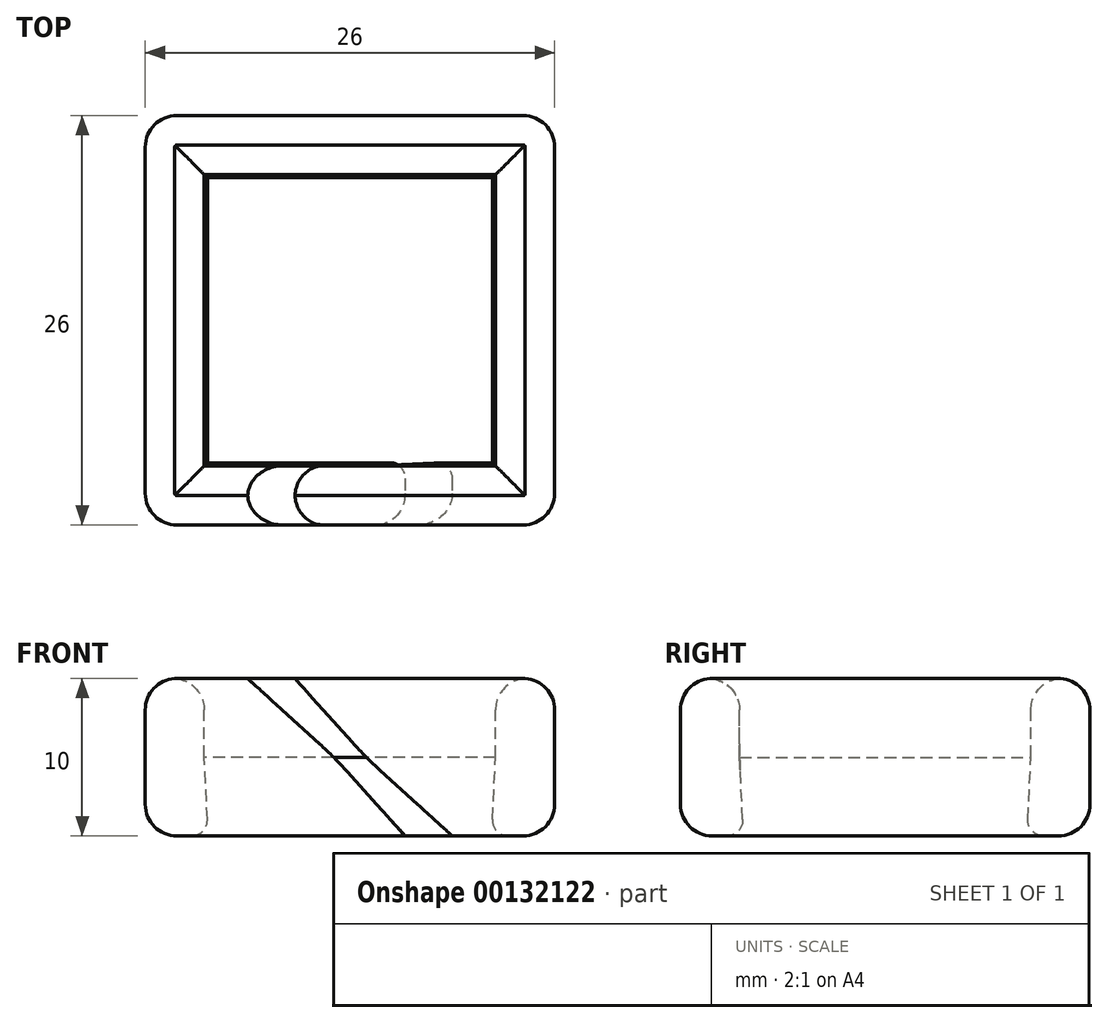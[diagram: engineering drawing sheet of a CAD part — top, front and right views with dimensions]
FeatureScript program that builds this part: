
annotation { "Feature Type Name" : "Feature", "Feature Type Description" : "" }
export const myFeature = defineFeature(function(context is Context, id is Id, definition is map)
    precondition{}
    {
        {
            var Q0;
            Q0=qCreatedBy(makeId("Top.planeOp"),FACE);
            var sketch = newSketch(context, id + "F0", { "sketchPlane" : qUnion([Q0])});
            skLineSegment(sketch, "E0.bottom", {"start": v(9, -9) * mm, "end": v(-9, -9) * mm});
            skLineSegment(sketch, "E0.top", {"start": v(9, 9) * mm, "end": v(-9, 9) * mm});
            skLineSegment(sketch, "E0.left", {"start": v(9, -9) * mm, "end": v(9, 9) * mm});
            skLineSegment(sketch, "E0.right", {"start": v(-9, -9) * mm, "end": v(-9, 9) * mm});
            skPoint(sketch, "E0.middle", {"position": v(0, 0) * mm});
            skLineSegment(sketch, "E1.bottom", {"start": v(13, -13) * mm, "end": v(-13, -13) * mm});
            skLineSegment(sketch, "E1.top", {"start": v(13, 13) * mm, "end": v(-13, 13) * mm});
            skLineSegment(sketch, "E1.left", {"start": v(13, -13) * mm, "end": v(13, 13) * mm});
            skLineSegment(sketch, "E1.right", {"start": v(-13, -13) * mm, "end": v(-13, 13) * mm});
            skLineSegment(sketch, "E2", {"start": v(-9, -9) * mm, "end": v(-13, -13) * mm});
            skLineSegment(sketch, "E3", {"start": v(9, 9) * mm, "end": v(13, 13) * mm});
            skLineSegment(sketch, "E4", {"start": v(0, -9) * mm, "end": v(0, -13) * mm, "construction": true});
            skLineSegment(sketch, "E5.0", {"start": v(5, -9) * mm, "end": v(5, -13) * mm, "construction": true});
            skLineSegment(sketch, "E6.0", {"start": v(6.5, -9) * mm, "end": v(6.5, -13) * mm});
            skLineSegment(sketch, "E7.0", {"start": v(3.5, -9) * mm, "end": v(3.5, -13) * mm});
            skSolve(sketch);
        }
        {
            var Q0;
            Q0=qCreatedBy(makeId("Top.planeOp"),FACE);
            cPlane(context, id + "F1", {"entities" : qUnion([Q0]), "cplaneType" : CPlaneType.OFFSET, "offset" : 5 * mm, "width" : 150 * mm, "height" : 150 * mm});
        }
        {
            var Q0;
            Q0=qCreatedBy(id+"F1.planeOp",FACE);
            var sketch = newSketch(context, id + "F2", { "sketchPlane" : qUnion([Q0])});
            skPoint(sketch, "E8.0", {"position": v(0, 0) * mm});
            skLineSegment(sketch, "E9.0", {"start": v(13, 13) * mm, "end": v(-13, 13) * mm});
            skLineSegment(sketch, "E10.0", {"start": v(-13, -13) * mm, "end": v(-13, 13) * mm});
            skLineSegment(sketch, "E11.0", {"start": v(13, -13) * mm, "end": v(-13, -13) * mm});
            skLineSegment(sketch, "E12.0", {"start": v(13, -13) * mm, "end": v(13, 13) * mm});
            skLineSegment(sketch, "E13.bottom", {"start": v(9.25, -9.25) * mm, "end": v(-9.25, -9.25) * mm});
            skLineSegment(sketch, "E13.top", {"start": v(9.25, 9.25) * mm, "end": v(-9.25, 9.25) * mm});
            skLineSegment(sketch, "E13.left", {"start": v(9.25, -9.25) * mm, "end": v(9.25, 9.25) * mm});
            skLineSegment(sketch, "E13.right", {"start": v(-9.25, -9.25) * mm, "end": v(-9.25, 9.25) * mm});
            skLineSegment(sketch, "E14", {"start": v(-13, -13) * mm, "end": v(-9.25, -9.25) * mm});
            skLineSegment(sketch, "E15", {"start": v(9.25, 9.25) * mm, "end": v(13, 13) * mm});
            skLineSegment(sketch, "E16", {"start": v(0, -9.25) * mm, "end": v(0, -13) * mm, "construction": true});
            skLineSegment(sketch, "E17.0", {"start": v(-1, -9.25) * mm, "end": v(-1, -13) * mm});
            skLineSegment(sketch, "E18.MirrorCS", {"start": v(1, -9.25) * mm, "end": v(1, -13) * mm});
            skSolve(sketch);
        }
        {
            var Q0;
            Q0=qCreatedBy(makeId("Top.planeOp"),FACE);
            cPlane(context, id + "F3", {"entities" : qUnion([Q0]), "cplaneType" : CPlaneType.OFFSET, "offset" : 10 * mm, "width" : 150 * mm, "height" : 150 * mm});
        }
        {
            var Q0;
            Q0=qCreatedBy(id+"F3.planeOp",FACE);
            var sketch = newSketch(context, id + "F4", { "sketchPlane" : qUnion([Q0])});
            skPoint(sketch, "E19.0", {"position": v(0, 0) * mm});
            skLineSegment(sketch, "E20.0", {"start": v(13, 13) * mm, "end": v(-13, 13) * mm});
            skLineSegment(sketch, "E21.0", {"start": v(13, -13) * mm, "end": v(13, 13) * mm});
            skLineSegment(sketch, "E21.1", {"start": v(13, -13) * mm, "end": v(-13, -13) * mm});
            skLineSegment(sketch, "E21.2", {"start": v(-13, -13) * mm, "end": v(-13, 13) * mm});
            skLineSegment(sketch, "E22.bottom", {"start": v(9.25, -9.25) * mm, "end": v(-9.25, -9.25) * mm});
            skLineSegment(sketch, "E22.top", {"start": v(9.25, 9.25) * mm, "end": v(-9.25, 9.25) * mm});
            skLineSegment(sketch, "E22.left", {"start": v(9.25, -9.25) * mm, "end": v(9.25, 9.25) * mm});
            skLineSegment(sketch, "E22.right", {"start": v(-9.25, -9.25) * mm, "end": v(-9.25, 9.25) * mm});
            skLineSegment(sketch, "E23", {"start": v(-13, -13) * mm, "end": v(-9.25, -9.25) * mm});
            skLineSegment(sketch, "E24", {"start": v(9.25, 9.25) * mm, "end": v(13, 13) * mm});
            skLineSegment(sketch, "E25", {"start": v(0, -9.25) * mm, "end": v(0, -13) * mm, "construction": true});
            skLineSegment(sketch, "E26.0", {"start": v(-5, -9.25) * mm, "end": v(-5, -13) * mm, "construction": true});
            skLineSegment(sketch, "E27.0", {"start": v(-6.5, -9.25) * mm, "end": v(-6.5, -13) * mm});
            skLineSegment(sketch, "E28.0", {"start": v(-3.5, -9.25) * mm, "end": v(-3.5, -13) * mm});
            skSolve(sketch);
        }
        {
            var Q0;
            Q0=makeQuery(id+"F0.imprint","IMPRINT",FACE,{"disambiguationData":[TD([[makeQuery(id+"F0.imprint","IMPRINT",EDGE,{"derivedFrom":sQuery(id+"F0.wireOp",EDGE,"E0.top")}),-1.0]])]});
            var Q1;
            Q1=makeQuery(id+"F2.imprint","IMPRINT",FACE,{"disambiguationData":[TD([[makeQuery(id+"F2.imprint","IMPRINT",EDGE,{"derivedFrom":sQuery(id+"F2.wireOp",EDGE,"E9.0")}),1.0]])]});
            loft(context, id + "F5", {"sheetProfilesArray" : [{ "sheetProfileEntities" : qUnion([Q0]) }, { "sheetProfileEntities" : qUnion([Q1]) }]});
        }
        {
            var Q1;
            Q1=makeQuery(id+"F2.imprint","IMPRINT",FACE,{"disambiguationData":[TD([[makeQuery(id+"F2.imprint","IMPRINT",EDGE,{"derivedFrom":sQuery(id+"F2.wireOp",EDGE,"E9.0")}),1.0]])]});
            var Q2;
            Q2=makeQuery(id+"F4.imprint","IMPRINT",FACE,{"disambiguationData":[TD([[makeQuery(id+"F4.imprint","IMPRINT",EDGE,{"derivedFrom":sQuery(id+"F4.wireOp",EDGE,"E20.0")}),1.0]])]});
            loft(context, id + "F6", {"operationType" : NewBodyOperationType.ADD, "sheetProfilesArray" : [{ "sheetProfileEntities" : qUnion([Q1]) }, { "sheetProfileEntities" : qUnion([Q2]) }]});
        }
        {
            var Q1;
            {var subQ0=sQuery(id+"F0.wireOp",EDGE,"E2");Q1=makeQuery(id+"F0.imprint","IMPRINT",FACE,{"disambiguationData":[TD([[makeQuery(id+"F0.imprint","IMPRINT",EDGE,{"derivedFrom":subQ0}),1.0]])]});}
            var Q2;
            {var subQ0=sQuery(id+"F2.wireOp",EDGE,"E14");Q2=makeQuery(id+"F2.imprint","IMPRINT",FACE,{"disambiguationData":[TD([[makeQuery(id+"F2.imprint","IMPRINT",EDGE,{"derivedFrom":subQ0}),-1.0]])]});}
            loft(context, id + "F7", {"operationType" : NewBodyOperationType.ADD, "sheetProfilesArray" : [{ "sheetProfileEntities" : qUnion([Q1]) }, { "sheetProfileEntities" : qUnion([Q2]) }]});
        }
        {
            var Q1;
            {var subQ0=sQuery(id+"F2.wireOp",EDGE,"E14");Q1=makeQuery(id+"F2.imprint","IMPRINT",FACE,{"disambiguationData":[TD([[makeQuery(id+"F2.imprint","IMPRINT",EDGE,{"derivedFrom":subQ0}),-1.0]])]});}
            var Q2;
            {var subQ0=sQuery(id+"F4.wireOp",EDGE,"E23");Q2=makeQuery(id+"F4.imprint","IMPRINT",FACE,{"disambiguationData":[TD([[makeQuery(id+"F4.imprint","IMPRINT",EDGE,{"derivedFrom":subQ0}),-1.0]])]});}
            loft(context, id + "F8", {"operationType" : NewBodyOperationType.ADD, "sheetProfilesArray" : [{ "sheetProfileEntities" : qUnion([Q1]) }, { "sheetProfileEntities" : qUnion([Q2]) }]});
        }
        {
            var Q1;
            {var subQ3=sQuery(id+"F0.wireOp",EDGE,"E0.left");Q1=makeQuery(id+"F0.imprint","IMPRINT",FACE,{"disambiguationData":[TD([[makeQuery(id+"F0.imprint","IMPRINT",EDGE,{"derivedFrom":subQ3}),-1.0]])]});}
            var Q2;
            {var subQ3=sQuery(id+"F2.wireOp",EDGE,"E12.0");Q2=makeQuery(id+"F2.imprint","IMPRINT",FACE,{"disambiguationData":[TD([[makeQuery(id+"F2.imprint","IMPRINT",EDGE,{"derivedFrom":subQ3}),1.0]])]});}
            loft(context, id + "F9", {"operationType" : NewBodyOperationType.ADD, "sheetProfilesArray" : [{ "sheetProfileEntities" : qUnion([Q1]) }, { "sheetProfileEntities" : qUnion([Q2]) }]});
        }
        {
            var Q1;
            {var subQ3=sQuery(id+"F2.wireOp",EDGE,"E12.0");Q1=makeQuery(id+"F2.imprint","IMPRINT",FACE,{"disambiguationData":[TD([[makeQuery(id+"F2.imprint","IMPRINT",EDGE,{"derivedFrom":subQ3}),1.0]])]});}
            var Q2;
            {var subQ4=sQuery(id+"F4.wireOp",EDGE,"E21.0");Q2=makeQuery(id+"F4.imprint","IMPRINT",FACE,{"disambiguationData":[TD([[makeQuery(id+"F4.imprint","IMPRINT",EDGE,{"derivedFrom":subQ4}),1.0]])]});}
            loft(context, id + "F10", {"operationType" : NewBodyOperationType.ADD, "sheetProfilesArray" : [{ "sheetProfileEntities" : qUnion([Q1]) }, { "sheetProfileEntities" : qUnion([Q2]) }]});
        }
        {
            var Q0;
            Q0=makeQuery(id+"F6.opLoft","MID_CAP_EDGE",EDGE,{"disambiguationData":[OSD([sQuery(id+"F4.wireOp",EDGE,"E22.top"),sQuery(id+"F4.wireOp",EDGE,"E22.left"),sQuery(id+"F4.wireOp",EDGE,"E22.right"),sQuery(id+"F4.wireOp",EDGE,"E24")])],"capPos":1.0});
            var Q1;
            Q1=makeQuery(id+"F10.opLoft","MID_CAP_EDGE",EDGE,{"disambiguationData":[OSD([sQuery(id+"F4.wireOp",EDGE,"E22.bottom"),sQuery(id+"F4.wireOp",EDGE,"E22.top"),sQuery(id+"F4.wireOp",EDGE,"E22.left"),sQuery(id+"F4.wireOp",EDGE,"E24")])],"capPos":1.0});
            var Q2;
            Q2=makeQuery(id+"F10.opLoft","MID_CAP_EDGE",EDGE,{"disambiguationData":[OSD([sQuery(id+"F4.wireOp",EDGE,"E22.bottom"),sQuery(id+"F4.wireOp",EDGE,"E22.left"),sQuery(id+"F4.wireOp",EDGE,"ebbac85e-4af3-46f9-9d82-f182fd674b780.MirrorCS")])],"capPos":1.0});
            var Q3;
            Q3=makeQuery(id+"F6.opLoft","MID_CAP_EDGE",EDGE,{"disambiguationData":[OSD([sQuery(id+"F4.wireOp",EDGE,"E22.bottom"),sQuery(id+"F4.wireOp",EDGE,"E22.top"),sQuery(id+"F4.wireOp",EDGE,"E22.right"),sQuery(id+"F4.wireOp",EDGE,"E23")])],"capPos":1.0});
            var Q4;
            Q4=makeQuery(id+"F8.opLoft","MID_CAP_EDGE",EDGE,{"disambiguationData":[OSD([sQuery(id+"F4.wireOp",EDGE,"E22.bottom"),sQuery(id+"F4.wireOp",EDGE,"E22.right"),sQuery(id+"F4.wireOp",EDGE,"E23"),sQuery(id+"F4.wireOp",EDGE,"E27.0")])],"capPos":1.0});
            var Q5;
            Q5=makeQuery(id+"F6.opLoft","MID_CAP_EDGE",EDGE,{"disambiguationData":[OSD([sQuery(id+"F4.wireOp",EDGE,"E20.0"),sQuery(id+"F4.wireOp",EDGE,"E21.1"),sQuery(id+"F4.wireOp",EDGE,"E21.2"),sQuery(id+"F4.wireOp",EDGE,"E23")])],"capPos":1.0});
            var Q6;
            Q6=makeQuery(id+"F8.opLoft","MID_CAP_EDGE",EDGE,{"disambiguationData":[OSD([sQuery(id+"F4.wireOp",EDGE,"E21.1"),sQuery(id+"F4.wireOp",EDGE,"E21.2"),sQuery(id+"F4.wireOp",EDGE,"E23"),sQuery(id+"F4.wireOp",EDGE,"E27.0")])],"capPos":1.0});
            var Q7;
            Q7=makeQuery(id+"F10.opLoft","MID_CAP_EDGE",EDGE,{"disambiguationData":[OSD([sQuery(id+"F4.wireOp",EDGE,"E21.0"),sQuery(id+"F4.wireOp",EDGE,"E21.1"),sQuery(id+"F4.wireOp",EDGE,"ebbac85e-4af3-46f9-9d82-f182fd674b780.MirrorCS")])],"capPos":1.0});
            var Q8;
            Q8=makeQuery(id+"F6.opLoft","MID_CAP_EDGE",EDGE,{"disambiguationData":[OSD([sQuery(id+"F4.wireOp",EDGE,"E20.0"),sQuery(id+"F4.wireOp",EDGE,"E21.0"),sQuery(id+"F4.wireOp",EDGE,"E21.2"),sQuery(id+"F4.wireOp",EDGE,"E24")])],"capPos":1.0});
            var Q9;
            Q9=makeQuery(id+"F10.opLoft","MID_CAP_EDGE",EDGE,{"disambiguationData":[OSD([sQuery(id+"F4.wireOp",EDGE,"E20.0"),sQuery(id+"F4.wireOp",EDGE,"E21.0"),sQuery(id+"F4.wireOp",EDGE,"E21.1"),sQuery(id+"F4.wireOp",EDGE,"E24")])],"capPos":1.0});
            var Q10;
            {var subQ0=sQuery(id+"F4.wireOp",EDGE,"E24");var subQ1=sQuery(id+"F4.wireOp",EDGE,"E21.0");var subQ2=sQuery(id+"F4.wireOp",EDGE,"E20.0");var subQ3=sQuery(id+"F2.wireOp",EDGE,"E15");var subQ4=sQuery(id+"F2.wireOp",EDGE,"E12.0");var subQ5=sQuery(id+"F2.wireOp",EDGE,"E9.0");var subQ6=sQuery(id+"F0.wireOp",EDGE,"E3");var subQ7=sQuery(id+"F0.wireOp",EDGE,"E1.left");var subQ8=sQuery(id+"F0.wireOp",EDGE,"E1.top");var subQ9=makeQuery(id+"F6.boolean.opBoolean","MERGE",EDGE,{"derivedFrom":[makeQuery(id+"F5.opLoft","SWEPT_EDGE",EDGE,{"disambiguationData":[OSD([subQ8,subQ7,subQ6,subQ5,subQ4,subQ3])]}),makeQuery(id+"F6.opLoft","SWEPT_EDGE",EDGE,{"disambiguationData":[OSD([subQ5,subQ4,subQ3,subQ2,subQ1,subQ0])]})]});Q10=makeQuery(id+"F10.boolean.opBoolean","MERGE",EDGE,{"derivedFrom":[makeQuery(id+"F9.boolean.opBoolean","MERGE",EDGE,{"derivedFrom":[subQ9,makeQuery(id+"F9.opLoft","SWEPT_EDGE",EDGE,{"disambiguationData":[OSD([subQ8,subQ7,subQ6,subQ5,subQ4,subQ3])]})]}),makeQuery(id+"F9.boolean.opBoolean","SPLIT",EDGE,{"derivedFrom":subQ9}),makeQuery(id+"F10.opLoft","SWEPT_EDGE",EDGE,{"disambiguationData":[OSD([subQ5,subQ4,subQ3,subQ2,subQ1,subQ0])]})]});}
            var Q11;
            {var subQ0=sQuery(id+"F2.wireOp",EDGE,"E12.0");var subQ1=sQuery(id+"F2.wireOp",EDGE,"E11.0");Q11=makeQuery(id+"F10.boolean.opBoolean","MERGE",EDGE,{"derivedFrom":[makeQuery(id+"F9.opLoft","SWEPT_EDGE",EDGE,{"disambiguationData":[OSD([sQuery(id+"F0.wireOp",EDGE,"E1.bottom"),sQuery(id+"F0.wireOp",EDGE,"E1.left"),subQ1,subQ0])]}),makeQuery(id+"F10.opLoft","SWEPT_EDGE",EDGE,{"disambiguationData":[OSD([subQ1,subQ0,sQuery(id+"F4.wireOp",EDGE,"E21.0"),sQuery(id+"F4.wireOp",EDGE,"E21.1")])]})]});}
            var Q12;
            {var subQ0=sQuery(id+"F4.wireOp",EDGE,"E23");var subQ1=sQuery(id+"F4.wireOp",EDGE,"E21.2");var subQ2=sQuery(id+"F4.wireOp",EDGE,"E21.1");var subQ3=sQuery(id+"F2.wireOp",EDGE,"E14");var subQ4=sQuery(id+"F2.wireOp",EDGE,"E11.0");var subQ5=sQuery(id+"F2.wireOp",EDGE,"E10.0");var subQ6=sQuery(id+"F0.wireOp",EDGE,"E2");var subQ7=sQuery(id+"F0.wireOp",EDGE,"E1.right");var subQ8=sQuery(id+"F0.wireOp",EDGE,"E1.bottom");var subQ9=makeQuery(id+"F6.boolean.opBoolean","MERGE",EDGE,{"derivedFrom":[makeQuery(id+"F5.opLoft","SWEPT_EDGE",EDGE,{"disambiguationData":[OSD([subQ8,subQ7,subQ6,subQ5,subQ4,subQ3])]}),makeQuery(id+"F6.opLoft","SWEPT_EDGE",EDGE,{"disambiguationData":[OSD([subQ5,subQ4,subQ3,subQ2,subQ1,subQ0])]})]});Q12=makeQuery(id+"F8.boolean.opBoolean","MERGE",EDGE,{"derivedFrom":[makeQuery(id+"F7.boolean.opBoolean","MERGE",EDGE,{"derivedFrom":[subQ9,makeQuery(id+"F7.opLoft","SWEPT_EDGE",EDGE,{"disambiguationData":[OSD([subQ8,subQ7,subQ6,subQ5,subQ4,subQ3])]})]}),makeQuery(id+"F7.boolean.opBoolean","SPLIT",EDGE,{"derivedFrom":subQ9}),makeQuery(id+"F8.opLoft","SWEPT_EDGE",EDGE,{"disambiguationData":[OSD([subQ5,subQ4,subQ3,subQ2,subQ1,subQ0])]})]});}
            var Q13;
            Q13=makeQuery(id+"F9.opLoft","MID_CAP_EDGE",EDGE,{"disambiguationData":[OSD([sQuery(id+"F0.wireOp",EDGE,"E1.bottom"),sQuery(id+"F0.wireOp",EDGE,"E1.top"),sQuery(id+"F0.wireOp",EDGE,"E1.left"),sQuery(id+"F0.wireOp",EDGE,"E3")])],"capPos":0.0});
            var Q14;
            Q14=makeQuery(id+"F5.opLoft","MID_CAP_EDGE",EDGE,{"disambiguationData":[OSD([sQuery(id+"F0.wireOp",EDGE,"E1.top"),sQuery(id+"F0.wireOp",EDGE,"E1.left"),sQuery(id+"F0.wireOp",EDGE,"E1.right"),sQuery(id+"F0.wireOp",EDGE,"E3")])],"capPos":0.0});
            var Q15;
            Q15=makeQuery(id+"F9.opLoft","MID_CAP_EDGE",EDGE,{"disambiguationData":[OSD([sQuery(id+"F0.wireOp",EDGE,"E1.bottom"),sQuery(id+"F0.wireOp",EDGE,"E1.left"),sQuery(id+"F0.wireOp",EDGE,"E6.0")])],"capPos":0.0});
            var Q16;
            Q16=makeQuery(id+"F7.opLoft","MID_CAP_EDGE",EDGE,{"disambiguationData":[OSD([sQuery(id+"F0.wireOp",EDGE,"E1.bottom"),sQuery(id+"F0.wireOp",EDGE,"E1.right"),sQuery(id+"F0.wireOp",EDGE,"E2"),sQuery(id+"F0.wireOp",EDGE,"4b8213a9-0e5b-4562-8142-2c595d69f7cd0.MirrorCS")])],"capPos":0.0});
            var Q17;
            {var subQ0=sQuery(id+"F2.wireOp",EDGE,"E10.0");var subQ1=sQuery(id+"F2.wireOp",EDGE,"E9.0");Q17=makeQuery(id+"F6.boolean.opBoolean","MERGE",EDGE,{"derivedFrom":[makeQuery(id+"F5.opLoft","SWEPT_EDGE",EDGE,{"disambiguationData":[OSD([sQuery(id+"F0.wireOp",EDGE,"E1.top"),sQuery(id+"F0.wireOp",EDGE,"E1.right"),subQ1,subQ0])]}),makeQuery(id+"F6.opLoft","SWEPT_EDGE",EDGE,{"disambiguationData":[OSD([subQ1,subQ0,sQuery(id+"F4.wireOp",EDGE,"E20.0"),sQuery(id+"F4.wireOp",EDGE,"E21.2")])]})]});}
            var Q18;
            Q18=makeQuery(id+"F5.opLoft","MID_CAP_EDGE",EDGE,{"disambiguationData":[OSD([sQuery(id+"F0.wireOp",EDGE,"E1.bottom"),sQuery(id+"F0.wireOp",EDGE,"E1.top"),sQuery(id+"F0.wireOp",EDGE,"E1.right"),sQuery(id+"F0.wireOp",EDGE,"E2")])],"capPos":0.0});
            fillet(context, id + "F11", {"entities" : qUnion([Q0, Q1, Q2, Q3, Q4, Q5, Q6, Q7, Q8, Q9, Q10, Q11, Q12, Q13, Q14, Q15, Q16, Q17, Q18]), "radius" : 2 * mm, "tangentPropagation" : true, "allowEdgeOverflow" : false});
        }
        {
            var Q0;
            Q0=makeQuery(id+"F5.opLoft","MID_CAP_EDGE",EDGE,{"disambiguationData":[OSD([sQuery(id+"F0.wireOp",EDGE,"E0.top"),sQuery(id+"F0.wireOp",EDGE,"E0.left"),sQuery(id+"F0.wireOp",EDGE,"E0.right"),sQuery(id+"F0.wireOp",EDGE,"E3")])],"capPos":0.0});
            var Q1;
            Q1=makeQuery(id+"F5.opLoft","MID_CAP_EDGE",EDGE,{"disambiguationData":[OSD([sQuery(id+"F0.wireOp",EDGE,"E0.bottom"),sQuery(id+"F0.wireOp",EDGE,"E0.top"),sQuery(id+"F0.wireOp",EDGE,"E0.right"),sQuery(id+"F0.wireOp",EDGE,"E2")])],"capPos":0.0});
            var Q2;
            Q2=makeQuery(id+"F7.opLoft","MID_CAP_EDGE",EDGE,{"disambiguationData":[OSD([sQuery(id+"F0.wireOp",EDGE,"E0.bottom"),sQuery(id+"F0.wireOp",EDGE,"E0.right"),sQuery(id+"F0.wireOp",EDGE,"E2"),sQuery(id+"F0.wireOp",EDGE,"4b8213a9-0e5b-4562-8142-2c595d69f7cd0.MirrorCS")])],"capPos":0.0});
            var Q3;
            Q3=makeQuery(id+"F9.opLoft","MID_CAP_EDGE",EDGE,{"disambiguationData":[OSD([sQuery(id+"F0.wireOp",EDGE,"E0.bottom"),sQuery(id+"F0.wireOp",EDGE,"E0.top"),sQuery(id+"F0.wireOp",EDGE,"E0.left"),sQuery(id+"F0.wireOp",EDGE,"E3")])],"capPos":0.0});
            var Q4;
            Q4=makeQuery(id+"F9.opLoft","MID_CAP_EDGE",EDGE,{"disambiguationData":[OSD([sQuery(id+"F0.wireOp",EDGE,"E0.bottom"),sQuery(id+"F0.wireOp",EDGE,"E0.left"),sQuery(id+"F0.wireOp",EDGE,"E6.0")])],"capPos":0.0});
            fillet(context, id + "F12", {"entities" : qUnion([Q0, Q1, Q2, Q3, Q4]), "radius" : 1 * mm, "tangentPropagation" : true, "allowEdgeOverflow" : false});
        }
        {
            var Q0;
            {var subQ0=sQuery(id+"F2.wireOp",EDGE,"E17.0");var subQ1=sQuery(id+"F2.wireOp",EDGE,"E13.bottom");var subQ2=sQuery(id+"F2.wireOp",EDGE,"E11.0");Q0=makeQuery(id+"F8.boolean.opBoolean","MERGE",EDGE,{"derivedFrom":[makeQuery(id+"F7.opLoft","MID_CAP_EDGE",EDGE,{"disambiguationData":[OSD([subQ2,subQ1,subQ0])],"capPos":1.0}),makeQuery(id+"F8.opLoft","MID_CAP_EDGE",EDGE,{"disambiguationData":[OSD([subQ2,subQ1,subQ0])],"capPos":0.0})]});}
            var Q1;
            {var subQ0=sQuery(id+"F2.wireOp",EDGE,"E18.MirrorCS");var subQ1=sQuery(id+"F2.wireOp",EDGE,"E13.bottom");var subQ2=sQuery(id+"F2.wireOp",EDGE,"E11.0");Q1=makeQuery(id+"F10.boolean.opBoolean","MERGE",EDGE,{"derivedFrom":[makeQuery(id+"F9.opLoft","MID_CAP_EDGE",EDGE,{"disambiguationData":[OSD([subQ2,subQ1,subQ0])],"capPos":1.0}),makeQuery(id+"F10.opLoft","MID_CAP_EDGE",EDGE,{"disambiguationData":[OSD([subQ2,subQ1,subQ0])],"capPos":0.0})]});}
            fillet(context, id + "F13", {"entities" : qUnion([Q0, Q1]), "radius" : 25 * mm, "tangentPropagation" : true, "allowEdgeOverflow" : false});
        }
    });
